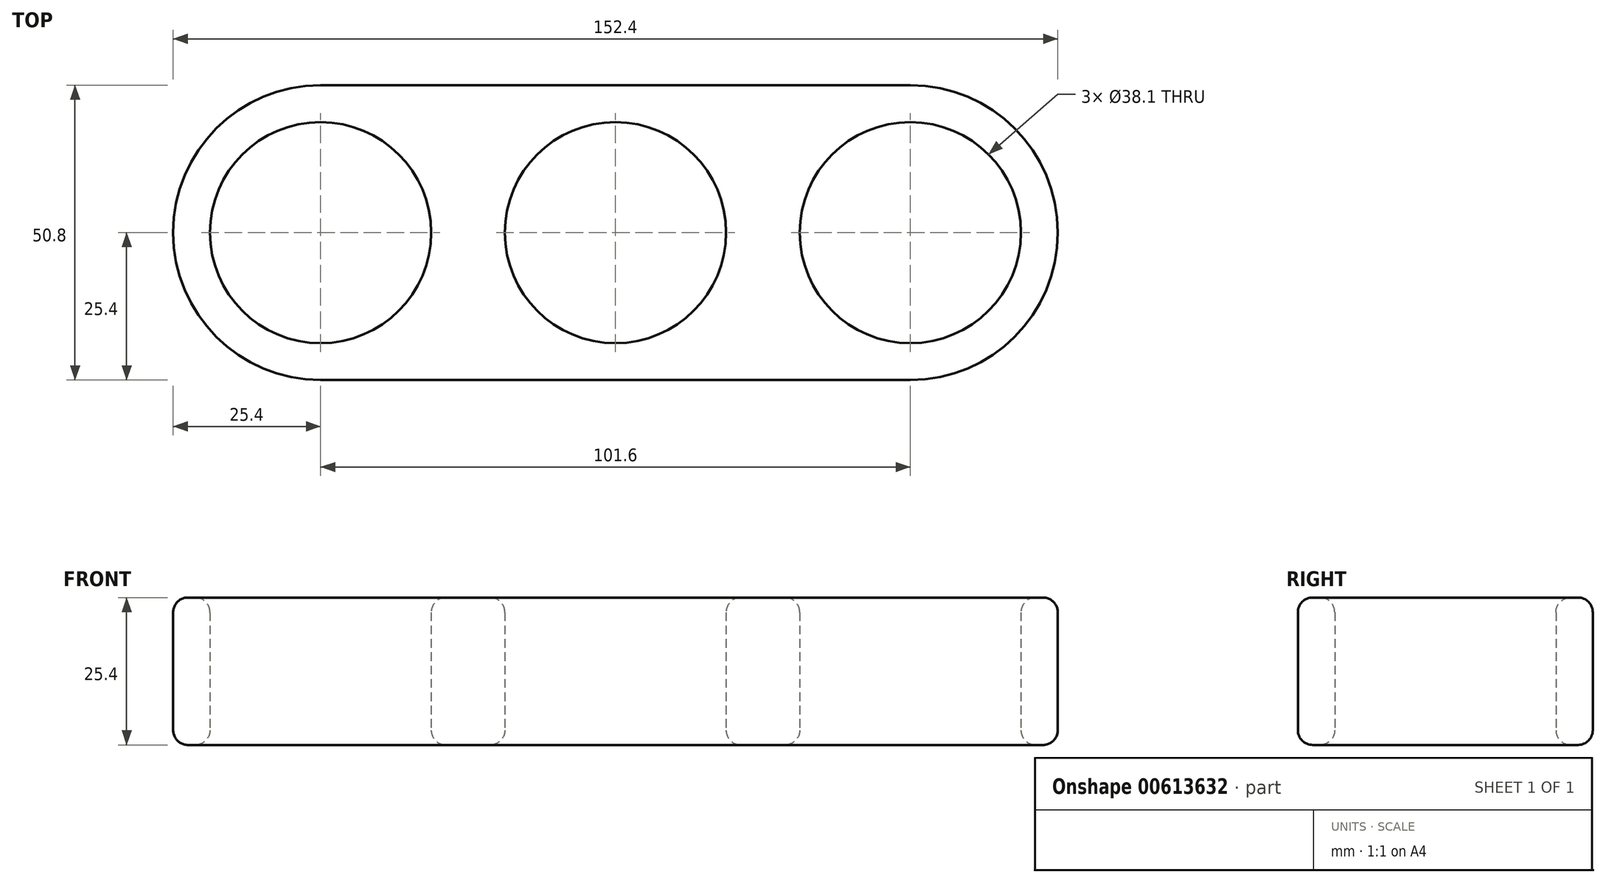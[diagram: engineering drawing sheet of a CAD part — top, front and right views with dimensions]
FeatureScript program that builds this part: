
annotation { "Feature Type Name" : "Feature", "Feature Type Description" : "" }
export const myFeature = defineFeature(function(context is Context, id is Id, definition is map)
    precondition{}
    {
        {
            var Q0;
            Q0=qCreatedBy(makeId("Top.planeOp"),FACE);
            var sketch = newSketch(context, id + "F0", { "sketchPlane" : qUnion([Q0])});
            skLineSegment(sketch, "E0.bottom", {"start": v(50.8, 25.4) * mm, "end": v(-50.8, 25.4) * mm});
            skLineSegment(sketch, "E0.top", {"start": v(50.8, -25.4) * mm, "end": v(-50.8, -25.4) * mm});
            skLineSegment(sketch, "E0.left", {"start": v(50.8, 25.4) * mm, "end": v(50.8, -25.4) * mm});
            skLineSegment(sketch, "E0.right", {"start": v(-50.8, 25.4) * mm, "end": v(-50.8, -25.4) * mm});
            skPoint(sketch, "E0.middle", {"position": v(0, 0) * mm});
            skCircle(sketch, "E1", {"center": v(-50.8, 0) * mm, "radius": 25.4 * mm});
            skCircle(sketch, "E2", {"center": v(0, 0) * mm, "radius": 25.4 * mm});
            skCircle(sketch, "E3", {"center": v(50.8, 0) * mm, "radius": 25.4 * mm});
            skCircle(sketch, "E4", {"center": v(-25.4, 0) * mm, "radius": 12.7 * mm});
            skCircle(sketch, "E5", {"center": v(25.4, 0) * mm, "radius": 12.7 * mm});
            skCircle(sketch, "E6", {"center": v(-50.8, 0) * mm, "radius": 19.05 * mm});
            skCircle(sketch, "E7", {"center": v(50.8, 0) * mm, "radius": 19.05 * mm});
            skCircle(sketch, "E8", {"center": v(0, 0) * mm, "radius": 19.05 * mm});
            skSolve(sketch);
        }
        {
            var Q0;
            {var subQ0=sQuery(id+"F0.wireOp",EDGE,"E0.left");Q0=makeQuery(id+"F0.imprint","IMPRINT",FACE,{"disambiguationData":[TD([[makeQuery(id+"F0.imprint","IMPRINT",EDGE,{"derivedFrom":subQ0}),1.0]])]});}
            var Q1;
            {var subQ1=sQuery(id+"F0.wireOp",EDGE,"E0.bottom");var subQ3=sQuery(id+"F0.wireOp",EDGE,"E2");var subQ4=makeQuery(id+"F0.imprint","INTERSECT",VERTEX,{"derivedFrom":[subQ1,subQ3]});Q1=makeQuery(id+"F0.imprint","IMPRINT",FACE,{"disambiguationData":[TD([[makeQuery(id+"F0.imprint","IMPRINT",EDGE,{"disambiguationData":[TD([[subQ4,1.0]])],"derivedFrom":subQ3}),-1.0]])]});}
            var Q2;
            {var subQ1=sQuery(id+"F0.wireOp",EDGE,"E0.top");var subQ3=sQuery(id+"F0.wireOp",EDGE,"E2");var subQ4=makeQuery(id+"F0.imprint","INTERSECT",VERTEX,{"derivedFrom":[subQ1,subQ3]});Q2=makeQuery(id+"F0.imprint","IMPRINT",FACE,{"disambiguationData":[TD([[makeQuery(id+"F0.imprint","IMPRINT",EDGE,{"disambiguationData":[TD([[subQ4,-1.0]])],"derivedFrom":subQ3}),-1.0]])]});}
            var Q3;
            {var subQ1=sQuery(id+"F0.wireOp",EDGE,"E0.top");var subQ3=sQuery(id+"F0.wireOp",EDGE,"E2");var subQ4=makeQuery(id+"F0.imprint","INTERSECT",VERTEX,{"derivedFrom":[subQ1,subQ3]});Q3=makeQuery(id+"F0.imprint","IMPRINT",FACE,{"disambiguationData":[TD([[makeQuery(id+"F0.imprint","IMPRINT",EDGE,{"disambiguationData":[TD([[subQ4,1.0]])],"derivedFrom":subQ3}),-1.0]])]});}
            var Q4;
            {var subQ2=sQuery(id+"F0.wireOp",EDGE,"E4");var subQ4=makeQuery(id+"F0.imprint","IMPRINT",VERTEX,{"derivedFrom":subQ2});Q4=makeQuery(id+"F0.imprint","IMPRINT",FACE,{"disambiguationData":[TD([[makeQuery(id+"F0.imprint","IMPRINT",EDGE,{"disambiguationData":[TD([[subQ4,-1.0]])],"derivedFrom":subQ2}),1.0]])]});}
            var Q5;
            {var subQ0=sQuery(id+"F0.wireOp",EDGE,"E4");var subQ1=sQuery(id+"F0.wireOp",EDGE,"E1");var subQ2=makeQuery(id+"F0.imprint","INTERSECT",VERTEX,{"disambiguationData":[OD(0.0)],"derivedFrom":[subQ1,subQ0]});Q5=makeQuery(id+"F0.imprint","IMPRINT",FACE,{"disambiguationData":[TD([[makeQuery(id+"F0.imprint","IMPRINT",EDGE,{"disambiguationData":[TD([[subQ2,1.0]])],"derivedFrom":subQ1}),1.0]])]});}
            var Q6;
            {var subQ0=sQuery(id+"F0.wireOp",EDGE,"E4");var subQ1=sQuery(id+"F0.wireOp",EDGE,"E1");var subQ2=makeQuery(id+"F0.imprint","INTERSECT",VERTEX,{"disambiguationData":[OD(0.0)],"derivedFrom":[subQ1,subQ0]});Q6=makeQuery(id+"F0.imprint","IMPRINT",FACE,{"disambiguationData":[TD([[makeQuery(id+"F0.imprint","IMPRINT",EDGE,{"disambiguationData":[TD([[subQ2,1.0]])],"derivedFrom":subQ1}),-1.0]])]});}
            var Q7;
            {var subQ1=sQuery(id+"F0.wireOp",EDGE,"E0.bottom");var subQ3=sQuery(id+"F0.wireOp",EDGE,"E2");var subQ4=makeQuery(id+"F0.imprint","INTERSECT",VERTEX,{"derivedFrom":[subQ1,subQ3]});Q7=makeQuery(id+"F0.imprint","IMPRINT",FACE,{"disambiguationData":[TD([[makeQuery(id+"F0.imprint","IMPRINT",EDGE,{"disambiguationData":[TD([[subQ4,-1.0]])],"derivedFrom":subQ3}),-1.0]])]});}
            var Q8;
            {var subQ0=sQuery(id+"F0.wireOp",EDGE,"E2");var subQ1=sQuery(id+"F0.wireOp",EDGE,"E1");var subQ2=makeQuery(id+"F0.imprint","INTERSECT",VERTEX,{"derivedFrom":[subQ1,subQ0]});Q8=makeQuery(id+"F0.imprint","IMPRINT",FACE,{"disambiguationData":[TD([[makeQuery(id+"F0.imprint","IMPRINT",EDGE,{"disambiguationData":[TD([[subQ2,1.0]])],"derivedFrom":subQ1}),-1.0]])]});}
            var Q9;
            {var subQ0=sQuery(id+"F0.wireOp",EDGE,"E3");var subQ1=sQuery(id+"F0.wireOp",EDGE,"E2");var subQ2=makeQuery(id+"F0.imprint","INTERSECT",VERTEX,{"derivedFrom":[subQ1,subQ0]});Q9=makeQuery(id+"F0.imprint","IMPRINT",FACE,{"disambiguationData":[TD([[makeQuery(id+"F0.imprint","IMPRINT",EDGE,{"disambiguationData":[TD([[subQ2,1.0]])],"derivedFrom":subQ1}),-1.0]])]});}
            var Q10;
            {var subQ0=sQuery(id+"F0.wireOp",EDGE,"E0.right");Q10=makeQuery(id+"F0.imprint","IMPRINT",FACE,{"disambiguationData":[TD([[makeQuery(id+"F0.imprint","IMPRINT",EDGE,{"derivedFrom":subQ0}),-1.0]])]});}
            var Q11;
            {var subQ0=sQuery(id+"F0.wireOp",EDGE,"E5");var subQ1=sQuery(id+"F0.wireOp",EDGE,"E2");var subQ2=makeQuery(id+"F0.imprint","INTERSECT",VERTEX,{"disambiguationData":[OD(0.0)],"derivedFrom":[subQ1,subQ0]});Q11=makeQuery(id+"F0.imprint","IMPRINT",FACE,{"disambiguationData":[TD([[makeQuery(id+"F0.imprint","IMPRINT",EDGE,{"disambiguationData":[TD([[subQ2,1.0]])],"derivedFrom":subQ1}),1.0]])]});}
            var Q12;
            {var subQ2=sQuery(id+"F0.wireOp",EDGE,"E5");var subQ5=makeQuery(id+"F0.imprint","IMPRINT",VERTEX,{"derivedFrom":subQ2});Q12=makeQuery(id+"F0.imprint","IMPRINT",FACE,{"disambiguationData":[TD([[makeQuery(id+"F0.imprint","IMPRINT",EDGE,{"disambiguationData":[TD([[subQ5,-1.0]])],"derivedFrom":subQ2}),1.0]])]});}
            var Q13;
            {var subQ0=sQuery(id+"F0.wireOp",EDGE,"E5");var subQ1=sQuery(id+"F0.wireOp",EDGE,"E2");var subQ2=makeQuery(id+"F0.imprint","INTERSECT",VERTEX,{"disambiguationData":[OD(0.0)],"derivedFrom":[subQ1,subQ0]});Q13=makeQuery(id+"F0.imprint","IMPRINT",FACE,{"disambiguationData":[TD([[makeQuery(id+"F0.imprint","IMPRINT",EDGE,{"disambiguationData":[TD([[subQ2,1.0]])],"derivedFrom":subQ1}),-1.0]])]});}
            var Q14;
            {var subQ0=sQuery(id+"F0.wireOp",EDGE,"E1");var subQ5=sQuery(id+"F0.wireOp",EDGE,"E4");var subQ6=makeQuery(id+"F0.imprint","INTERSECT",VERTEX,{"disambiguationData":[OD(0.0)],"derivedFrom":[subQ0,subQ5]});Q14=makeQuery(id+"F0.imprint","IMPRINT",FACE,{"disambiguationData":[TD([[makeQuery(id+"F0.imprint","IMPRINT",EDGE,{"disambiguationData":[TD([[subQ6,-1.0]])],"derivedFrom":subQ5}),-1.0]])]});}
            var Q15;
            {var subQ0=sQuery(id+"F0.wireOp",EDGE,"E6");var subQ4=makeQuery(id+"F0.imprint","IMPRINT",VERTEX,{"derivedFrom":subQ0});Q15=makeQuery(id+"F0.imprint","IMPRINT",FACE,{"disambiguationData":[TD([[makeQuery(id+"F0.imprint","IMPRINT",EDGE,{"disambiguationData":[TD([[subQ4,-1.0]])],"derivedFrom":subQ0}),1.0]])]});}
            var Q16;
            {var subQ1=sQuery(id+"F0.wireOp",EDGE,"E3");var subQ5=makeQuery(id+"F0.imprint","INTERSECT",VERTEX,{"derivedFrom":[sQuery(id+"F0.wireOp",EDGE,"E2"),subQ1]});Q16=makeQuery(id+"F0.imprint","IMPRINT",FACE,{"disambiguationData":[TD([[makeQuery(id+"F0.imprint","IMPRINT",EDGE,{"disambiguationData":[TD([[subQ5,1.0]])],"derivedFrom":subQ1}),1.0]])]});}
            var Q17;
            {var subQ0=sQuery(id+"F0.wireOp",EDGE,"E3");var subQ5=sQuery(id+"F0.wireOp",EDGE,"E5");var subQ6=makeQuery(id+"F0.imprint","INTERSECT",VERTEX,{"disambiguationData":[OD(1.0)],"derivedFrom":[subQ0,subQ5]});Q17=makeQuery(id+"F0.imprint","IMPRINT",FACE,{"disambiguationData":[TD([[makeQuery(id+"F0.imprint","IMPRINT",EDGE,{"disambiguationData":[TD([[subQ6,-1.0]])],"derivedFrom":subQ5}),-1.0]])]});}
            var Q18;
            {var subQ0=sQuery(id+"F0.wireOp",EDGE,"E1");var subQ5=sQuery(id+"F0.wireOp",EDGE,"E4");var subQ6=makeQuery(id+"F0.imprint","INTERSECT",VERTEX,{"disambiguationData":[OD(1.0)],"derivedFrom":[subQ0,subQ5]});Q18=makeQuery(id+"F0.imprint","IMPRINT",FACE,{"disambiguationData":[TD([[makeQuery(id+"F0.imprint","IMPRINT",EDGE,{"disambiguationData":[TD([[subQ6,1.0]])],"derivedFrom":subQ5}),-1.0]])]});}
            var Q19;
            {var subQ0=sQuery(id+"F0.wireOp",EDGE,"E3");var subQ5=sQuery(id+"F0.wireOp",EDGE,"E5");var subQ6=makeQuery(id+"F0.imprint","INTERSECT",VERTEX,{"disambiguationData":[OD(0.0)],"derivedFrom":[subQ0,subQ5]});Q19=makeQuery(id+"F0.imprint","IMPRINT",FACE,{"disambiguationData":[TD([[makeQuery(id+"F0.imprint","IMPRINT",EDGE,{"disambiguationData":[TD([[subQ6,1.0]])],"derivedFrom":subQ5}),-1.0]])]});}
            var Q20;
            {var subQ1=sQuery(id+"F0.wireOp",EDGE,"E2");var subQ5=makeQuery(id+"F0.imprint","INTERSECT",VERTEX,{"derivedFrom":[sQuery(id+"F0.wireOp",EDGE,"E0.top"),subQ1]});Q20=makeQuery(id+"F0.imprint","IMPRINT",FACE,{"disambiguationData":[TD([[makeQuery(id+"F0.imprint","IMPRINT",EDGE,{"disambiguationData":[TD([[subQ5,1.0]])],"derivedFrom":subQ1}),1.0]])]});}
            var Q21;
            {var subQ1=sQuery(id+"F0.wireOp",EDGE,"E2");var subQ8=makeQuery(id+"F0.imprint","INTERSECT",VERTEX,{"derivedFrom":[sQuery(id+"F0.wireOp",EDGE,"E0.bottom"),subQ1]});Q21=makeQuery(id+"F0.imprint","IMPRINT",FACE,{"disambiguationData":[TD([[makeQuery(id+"F0.imprint","IMPRINT",EDGE,{"disambiguationData":[TD([[subQ8,1.0]])],"derivedFrom":subQ1}),1.0]])]});}
            var Q22;
            {var subQ0=sQuery(id+"F0.wireOp",EDGE,"E8");var subQ4=makeQuery(id+"F0.imprint","IMPRINT",VERTEX,{"derivedFrom":subQ0});Q22=makeQuery(id+"F0.imprint","IMPRINT",FACE,{"disambiguationData":[TD([[makeQuery(id+"F0.imprint","IMPRINT",EDGE,{"disambiguationData":[TD([[subQ4,-1.0]])],"derivedFrom":subQ0}),1.0]])]});}
            var Q23;
            {var subQ1=sQuery(id+"F0.wireOp",EDGE,"E2");var subQ7=makeQuery(id+"F0.imprint","INTERSECT",VERTEX,{"derivedFrom":[sQuery(id+"F0.wireOp",EDGE,"E1"),subQ1]});Q23=makeQuery(id+"F0.imprint","IMPRINT",FACE,{"disambiguationData":[TD([[makeQuery(id+"F0.imprint","IMPRINT",EDGE,{"disambiguationData":[TD([[subQ7,1.0]])],"derivedFrom":subQ1}),1.0]])]});}
            extrude(context, id + "F1", {"entities" : qUnion([Q0, Q1, Q2, Q3, Q4, Q5, Q6, Q7, Q8, Q9, Q10, Q11, Q12, Q13, Q14, Q15, Q16, Q17, Q18, Q19, Q20, Q21, Q22, Q23]), "depth" : 25.4 * mm, "offsetDistance" : 25.4 * mm});
        }
        {
            var Q0;
            Q0=makeQuery(id+"F1.opExtrude","CAP_EDGE",EDGE,{"disambiguationData":[OSD([sQuery(id+"F0.wireOp",EDGE,"E1")])],"isStart":false});
            var Q1;
            Q1=makeQuery(id+"F1.opExtrude","CAP_EDGE",EDGE,{"disambiguationData":[OSD([sQuery(id+"F0.wireOp",EDGE,"E1")])],"isStart":true});
            var Q2;
            Q2=makeQuery(id+"F1.opExtrude","CAP_EDGE",EDGE,{"disambiguationData":[OSD([sQuery(id+"F0.wireOp",EDGE,"E6")])],"isStart":false});
            var Q3;
            {var subQ0=sQuery(id+"F0.wireOp",EDGE,"E8");Q3=makeQuery(id+"F1.opExtrude","CAP_EDGE",EDGE,{"disambiguationData":[OSD([subQ0]),TDD([makeQuery(id+"F0.imprint","IMPRINT",EDGE,{"disambiguationData":[TD([[makeQuery(id+"F0.imprint","INTERSECT",VERTEX,{"disambiguationData":[OD(0.0)],"derivedFrom":[sQuery(id+"F0.wireOp",EDGE,"E4"),subQ0]}),1.0]])],"derivedFrom":subQ0})])],"isStart":false});}
            var Q4;
            {var subQ0=sQuery(id+"F0.wireOp",EDGE,"E4");var subQ1=makeQuery(id+"F0.imprint","IMPRINT",VERTEX,{"derivedFrom":subQ0});Q4=makeQuery(id+"F1.opExtrude","CAP_EDGE",EDGE,{"disambiguationData":[OSD([subQ0]),TDD([makeQuery(id+"F0.imprint","IMPRINT",EDGE,{"disambiguationData":[TD([[subQ1,-1.0]])],"derivedFrom":subQ0}),makeQuery(id+"F0.imprint","IMPRINT",EDGE,{"disambiguationData":[TD([[subQ1,1.0]])],"derivedFrom":subQ0})])],"isStart":false});}
            var Q5;
            {var subQ0=sQuery(id+"F0.wireOp",EDGE,"E8");var subQ1=sQuery(id+"F0.wireOp",EDGE,"E5");Q5=makeQuery(id+"F1.opExtrude","CAP_EDGE",EDGE,{"disambiguationData":[OSD([subQ1]),TDD([makeQuery(id+"F0.imprint","IMPRINT",EDGE,{"disambiguationData":[TD([[makeQuery(id+"F0.imprint","INTERSECT",VERTEX,{"disambiguationData":[OD(0.0)],"derivedFrom":[subQ1,subQ0]}),-1.0]])],"derivedFrom":subQ1})])],"isStart":false});}
            var Q6;
            {var subQ0=sQuery(id+"F0.wireOp",EDGE,"E8");Q6=makeQuery(id+"F1.opExtrude","CAP_EDGE",EDGE,{"disambiguationData":[OSD([subQ0]),TDD([makeQuery(id+"F0.imprint","IMPRINT",EDGE,{"disambiguationData":[TD([[makeQuery(id+"F0.imprint","INTERSECT",VERTEX,{"disambiguationData":[OD(1.0)],"derivedFrom":[sQuery(id+"F0.wireOp",EDGE,"E4"),subQ0]}),-1.0]])],"derivedFrom":subQ0})])],"isStart":false});}
            var Q7;
            {var subQ0=sQuery(id+"F0.wireOp",EDGE,"E5");var subQ1=makeQuery(id+"F0.imprint","IMPRINT",VERTEX,{"derivedFrom":subQ0});Q7=makeQuery(id+"F1.opExtrude","CAP_EDGE",EDGE,{"disambiguationData":[OSD([subQ0]),TDD([makeQuery(id+"F0.imprint","IMPRINT",EDGE,{"disambiguationData":[TD([[subQ1,-1.0]])],"derivedFrom":subQ0}),makeQuery(id+"F0.imprint","IMPRINT",EDGE,{"disambiguationData":[TD([[subQ1,1.0]])],"derivedFrom":subQ0})])],"isStart":false});}
            var Q8;
            Q8=makeQuery(id+"F1.opExtrude","CAP_EDGE",EDGE,{"disambiguationData":[OSD([sQuery(id+"F0.wireOp",EDGE,"E7")])],"isStart":false});
            var Q9;
            {var subQ0=sQuery(id+"F0.wireOp",EDGE,"E6");var subQ1=sQuery(id+"F0.wireOp",EDGE,"E4");Q9=makeQuery(id+"F1.opExtrude","CAP_EDGE",EDGE,{"disambiguationData":[OSD([subQ1]),TDD([makeQuery(id+"F0.imprint","IMPRINT",EDGE,{"disambiguationData":[TD([[makeQuery(id+"F0.imprint","INTERSECT",VERTEX,{"disambiguationData":[OD(0.0)],"derivedFrom":[subQ1,subQ0]}),-1.0]])],"derivedFrom":subQ1})])],"isStart":false});}
            var Q10;
            Q10=makeQuery(id+"F1.opExtrude","CAP_EDGE",EDGE,{"disambiguationData":[OSD([sQuery(id+"F0.wireOp",EDGE,"E7")])],"isStart":true});
            var Q11;
            {var subQ0=sQuery(id+"F0.wireOp",EDGE,"E5");var subQ1=makeQuery(id+"F0.imprint","IMPRINT",VERTEX,{"derivedFrom":subQ0});Q11=makeQuery(id+"F1.opExtrude","CAP_EDGE",EDGE,{"disambiguationData":[OSD([subQ0]),TDD([makeQuery(id+"F0.imprint","IMPRINT",EDGE,{"disambiguationData":[TD([[subQ1,-1.0]])],"derivedFrom":subQ0}),makeQuery(id+"F0.imprint","IMPRINT",EDGE,{"disambiguationData":[TD([[subQ1,1.0]])],"derivedFrom":subQ0})])],"isStart":true});}
            var Q12;
            {var subQ0=sQuery(id+"F0.wireOp",EDGE,"E8");var subQ1=sQuery(id+"F0.wireOp",EDGE,"E5");Q12=makeQuery(id+"F1.opExtrude","CAP_EDGE",EDGE,{"disambiguationData":[OSD([subQ1]),TDD([makeQuery(id+"F0.imprint","IMPRINT",EDGE,{"disambiguationData":[TD([[makeQuery(id+"F0.imprint","INTERSECT",VERTEX,{"disambiguationData":[OD(0.0)],"derivedFrom":[subQ1,subQ0]}),-1.0]])],"derivedFrom":subQ1})])],"isStart":true});}
            var Q13;
            {var subQ0=sQuery(id+"F0.wireOp",EDGE,"E8");Q13=makeQuery(id+"F1.opExtrude","CAP_EDGE",EDGE,{"disambiguationData":[OSD([subQ0]),TDD([makeQuery(id+"F0.imprint","IMPRINT",EDGE,{"disambiguationData":[TD([[makeQuery(id+"F0.imprint","INTERSECT",VERTEX,{"disambiguationData":[OD(0.0)],"derivedFrom":[sQuery(id+"F0.wireOp",EDGE,"E4"),subQ0]}),1.0]])],"derivedFrom":subQ0})])],"isStart":true});}
            var Q14;
            {var subQ0=sQuery(id+"F0.wireOp",EDGE,"E8");Q14=makeQuery(id+"F1.opExtrude","CAP_EDGE",EDGE,{"disambiguationData":[OSD([subQ0]),TDD([makeQuery(id+"F0.imprint","IMPRINT",EDGE,{"disambiguationData":[TD([[makeQuery(id+"F0.imprint","INTERSECT",VERTEX,{"disambiguationData":[OD(1.0)],"derivedFrom":[sQuery(id+"F0.wireOp",EDGE,"E4"),subQ0]}),-1.0]])],"derivedFrom":subQ0})])],"isStart":true});}
            var Q15;
            {var subQ0=sQuery(id+"F0.wireOp",EDGE,"E4");var subQ1=makeQuery(id+"F0.imprint","IMPRINT",VERTEX,{"derivedFrom":subQ0});Q15=makeQuery(id+"F1.opExtrude","CAP_EDGE",EDGE,{"disambiguationData":[OSD([subQ0]),TDD([makeQuery(id+"F0.imprint","IMPRINT",EDGE,{"disambiguationData":[TD([[subQ1,-1.0]])],"derivedFrom":subQ0}),makeQuery(id+"F0.imprint","IMPRINT",EDGE,{"disambiguationData":[TD([[subQ1,1.0]])],"derivedFrom":subQ0})])],"isStart":true});}
            var Q16;
            {var subQ0=sQuery(id+"F0.wireOp",EDGE,"E6");var subQ1=sQuery(id+"F0.wireOp",EDGE,"E4");Q16=makeQuery(id+"F1.opExtrude","CAP_EDGE",EDGE,{"disambiguationData":[OSD([subQ1]),TDD([makeQuery(id+"F0.imprint","IMPRINT",EDGE,{"disambiguationData":[TD([[makeQuery(id+"F0.imprint","INTERSECT",VERTEX,{"disambiguationData":[OD(0.0)],"derivedFrom":[subQ1,subQ0]}),-1.0]])],"derivedFrom":subQ1})])],"isStart":true});}
            var Q17;
            Q17=makeQuery(id+"F1.opExtrude","CAP_EDGE",EDGE,{"disambiguationData":[OSD([sQuery(id+"F0.wireOp",EDGE,"E6")])],"isStart":true});
            fillet(context, id + "F2", {"entities" : qUnion([Q0, Q1, Q2, Q3, Q4, Q5, Q6, Q7, Q8, Q9, Q10, Q11, Q12, Q13, Q14, Q15, Q16, Q17]), "tangentPropagation" : true, "radius" : 2.54 * mm, "defaultsChanged" : false, "vertexSettings" : [], "allowEdgeOverflow" : false});
        }
    });
